# Revit family: BL4 C AP Sans hôte
name_source: partatom
category: Dispositifs d'éclairage
units: mm (PartAtom-declared; Revit-internal decimal feet)

## family parameters
Basée sur le plan de construction = Oui
Conserver l'orientation des annotations = Non
Cote de connecteur circulaire = Utiliser le diamètre
Couper avec des vides une fois chargée = Non
Partagée = Non
Point de calcul de pièce = Non
Toujours verticalement = Oui
Type d'élément = Normal

## types (1)
- BL4 C AP réf 93284
    Alimentation = 110-240 V AC
    Charge Cos ɸ =0.5 = 500 VA
    Charge Cos ɸ =1 = 1000 W
    Charge LED = 200 W
    Classe = II
    Code d'assemblage = D5010200
    Commentaires du type = DET.MOUV.SPECIAL COULOIR.1 CONTACT.180/360°/2x8M APPARENT
    Consommation = 0.30 W
    Elévation par défaut = 0 cm
    Fabricant = B.E.G.
    Hauteur de montage max = 280 cm
    IP = 20
    Image du type = COULOIR.jpg
    Marque = LUXOMAT
    Mode de pose = Saillie
    Modèle = BL4 C AP
    Relais = 4.3 A
    Référence = 93284+93183
    Température ambiante = -25°C à +50°C
    Type de Sortie = TOR
    URL = http://www.luxomat.com
